# Revit family: PRD_FrankeWS_Snks_SIRIUSUtilitySink_BS302_BS303
name_source: partatom
category: Plumbing Fixtures
revit_build: Autodesk Revit 2018 (Build: 20190510_1515(x64)
units: mm (PartAtom-declared; Revit-internal decimal feet)

## family parameters
Cut with Voids When Loaded = Yes
Host = Face
OmniClass Number = 23.45.05.14.14.27
OmniClass Title = Service Sinks
Part Type = Normal
Room Calculation Point = No
Round Connector Dimension = Use Diameter
Shared = Yes

## types (2) — shared parameters
AssetType = Fixed
BowlConstruction = Radius corners
BowlDepth = 320
BowlFinish = Satin finish
BowlHeight = 175
BowlPosition = Center
BowlWidth = 420
Brushes = Without brushes
Category = Pr_40_20_96_81, Sinks
Default Elevation = 925 mm  [stored 3.03478 ft]
DiameterNominal = 40  [stored 0.131234 ft]
DrainSize = 40 mm  [stored 0.131234 ft]
DrainerOrStorage = No
DurationUnit = year
Finish = Satin finished
FrameMaterial = PRD_AR_Plastic_GreyBlue
IfcExportAs = IfcSanitaryTerminalType
IfcExportType = SINK
IntegralAccessories = includes mounting material and mounting brackets loose
Manufacturer = KWC Group AG
ManufacturerName = KWC Group AG
ManufacturerURL = www.kwc.com
Material = Stainless steel
MaterialCode = 1.4301 Chrome Nickel steel V2A
MaterialThickness = 1.20 mm
Mounting = WallHung
NBSDescription = Sinks
NBSReference = 45-35-70/344
NominalDepth = 400 mm  [stored 1.31234 ft]
NominalHeight = 215 mm
NominalWidth = 500 mm  [stored 1.64042 ft]
NumberOfWashPlaces = 1
NumberOfWasteHoles = 1
OutletSize = G 1 1/2 B
Overflow = No
ProductInformation = https://pim.kwc.com
RearUpstand = No
SinkMaterial = PRD_AR_StainlessSteel_SatinFinished
SinkType = London
Size = 500 x 215 x 400 mm (W x H x D)
Spillway = No
Splashback = Component of another part
SplashbackHeight = 40.00 mm
Sump = No
SumpBasket = No
TailorMade = No
TapLedge = No
TypeOfMounting = Wall mounting
TypeOfUtilitySink = Multi purpose sink
TypeOfWasteKit = Perforated waste
URL = www.kwc.com
Uniclass2015Code = Pr_40_20_96_81
Uniclass2015Title = Sinks
Uniclass2015Version = Products v1.17
Version = 1
WarrantyDurationUnit = year
WashRiffle = No
WasteHolePosition = Right back corner
WasteHoleProjection = 105.00 mm
WasteKitIncluded = Yes
WasteSize = DN 40
zero-valued in all types: MountingOffset

## per-type parameters (varying)
| type | BIMObjectName | Description | Features | Grid | GridMaterial | GridVisibility | GrossWeight | MaterialCodeGrid | ModelNumber | Name | NetWeight | ProductCode |
| BS302 | PRD_AR_Sinks_SIRIUSUtilitySink_BS302 | Sink, for wall mounting, stainless steel, surface satin finished, material thickness 1,2 mm, seamless welded bowl, without overflow, with 1 1/2" plug waste with plastic overflow pipe, drainage back right, without tap ledge, with rear upstand 40 mm, with hinged grate, includes mounting material, and mounting brackets loose. | stainless steel, surface satin finished, drainage back right, with hinged grate | Hinged | Stainless steel | Yes | 5.40 kg | 1.4301 Chrome Nickel steel V2A | 2000071903 | SIRIUS Utility sink BS302 | 5.10 kg | 207.0000.057 |
| BS303 | PRD_AR_Sinks_SIRIUSUtilitySink_BS303 | Sink, for wall mounting, stainless steel, surface satin finished, material thickness 1,2 mm, seamless welded bowl, without overflow, with 1 1/2" plug waste with plastic overflow pipe, drainage back right, without tap ledge, with rear upstand 40 mm, without hinged grate, includes mounting material and mounting brackets loose. | stainless steel, surface satin finished, drainage back right, without hinged grate | No |  | No | 5.06 kg |  | 2000090080 | SIRIUS Utility sink BS303 | 4.44 kg | 207.0483.166 |

note: column(s) folded — value = type name in every type: Model, ModelReference

note: [stored X ft] marks values corroborated as IEEE doubles in the binary element streams (Revit-internal decimal feet)

## geometry (parser evidence)
native form markers: Sweep x5
no freeform markers — native parametric forms only
